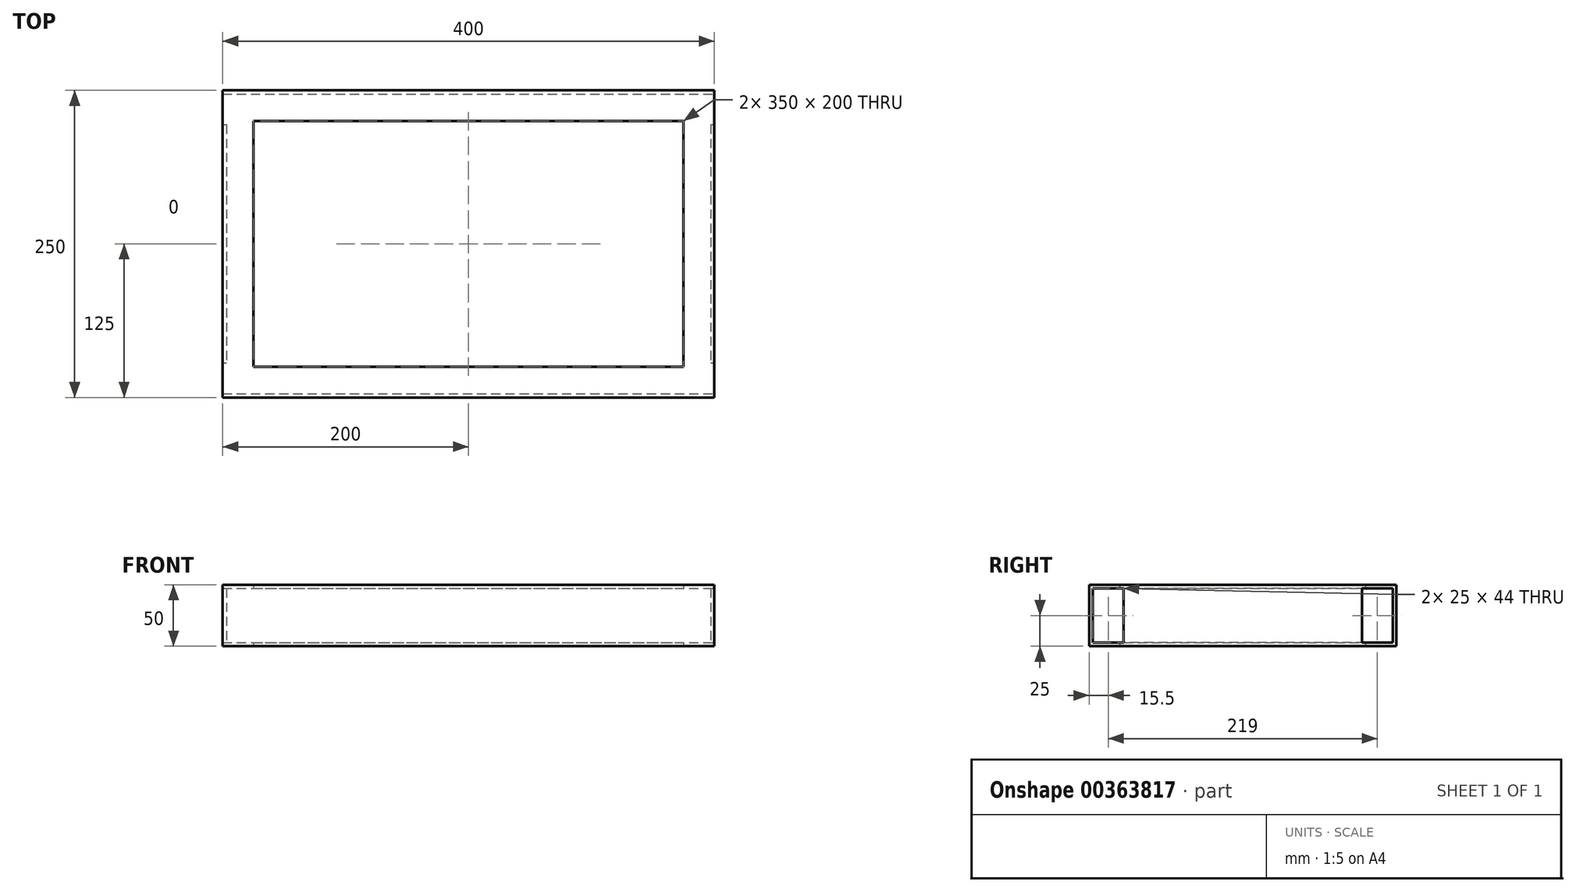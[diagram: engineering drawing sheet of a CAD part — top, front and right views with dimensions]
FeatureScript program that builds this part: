
annotation { "Feature Type Name" : "Feature", "Feature Type Description" : "" }
export const myFeature = defineFeature(function(context is Context, id is Id, definition is map)
    precondition{}
    {
        {
            var Q0;
            Q0=qCreatedBy(makeId("Top.planeOp"),FACE);
            var sketch = newSketch(context, id + "F0", { "sketchPlane" : qUnion([Q0])});
            skLineSegment(sketch, "E0.bottom", {"start": v(-200, 125) * mm, "end": v(200, 125) * mm});
            skLineSegment(sketch, "E0.top", {"start": v(-200, -125) * mm, "end": v(200, -125) * mm});
            skLineSegment(sketch, "E0.left", {"start": v(-200, 125) * mm, "end": v(-200, -125) * mm});
            skLineSegment(sketch, "E0.right", {"start": v(200, 125) * mm, "end": v(200, -125) * mm});
            skPoint(sketch, "E0.middle", {"position": v(0, 0) * mm});
            skLineSegment(sketch, "E1.bottom", {"start": v(-175, 100) * mm, "end": v(175, 100) * mm});
            skLineSegment(sketch, "E1.top", {"start": v(-175, -100) * mm, "end": v(175, -100) * mm});
            skLineSegment(sketch, "E1.left", {"start": v(-175, 100) * mm, "end": v(-175, -100) * mm});
            skLineSegment(sketch, "E1.right", {"start": v(175, 100) * mm, "end": v(175, -100) * mm});
            skLineSegment(sketch, "E2", {"start": v(-175, 33.87) * mm, "end": v(-200, 33.87) * mm, "construction": true});
            skLineSegment(sketch, "E3", {"start": v(-7.97, 100) * mm, "end": v(-7.97, 125) * mm, "construction": true});
            skLineSegment(sketch, "E4", {"start": v(-82.12, -100) * mm, "end": v(-82.12, -125) * mm, "construction": true});
            skLineSegment(sketch, "E5", {"start": v(175, -34.9) * mm, "end": v(200, -34.9) * mm, "construction": true});
            skSolve(sketch);
        }
        {
            var Q0;
            Q0=makeQuery(id+"F0.imprint","IMPRINT",FACE,{"disambiguationData":[TD([[makeQuery(id+"F0.imprint","IMPRINT",EDGE,{"derivedFrom":sQuery(id+"F0.wireOp",EDGE,"E0.bottom")}),-1.0]])]});
            extrude(context, id + "F1", {"entities" : qUnion([Q0]), "depth" : 50 * mm});
        }
        {
            var Q0;
            Q0=makeQuery(id+"F1.opExtrude","SWEPT_FACE",FACE,{"disambiguationData":[OSD([sQuery(id+"F0.wireOp",EDGE,"E0.top")])]});
            var sketch = newSketch(context, id + "F2", { "sketchPlane" : qUnion([Q0])});
            skLineSegment(sketch, "E6.bottom", {"start": v(197, 47) * mm, "end": v(172, 47) * mm});
            skLineSegment(sketch, "E6.top", {"start": v(197, 3) * mm, "end": v(172, 3) * mm});
            skLineSegment(sketch, "E6.left", {"start": v(197, 47) * mm, "end": v(197, 3) * mm});
            skLineSegment(sketch, "E6.right", {"start": v(172, 47) * mm, "end": v(172, 3) * mm});
            skLineSegment(sketch, "E7", {"start": v(197, 27.18) * mm, "end": v(200, 27.18) * mm, "construction": true});
            skLineSegment(sketch, "E8", {"start": v(108.69, 47) * mm, "end": v(108.69, 50) * mm, "construction": true});
            skLineSegment(sketch, "E9", {"start": v(106.18, 3) * mm, "end": v(106.18, 0) * mm, "construction": true});
            skLineSegment(sketch, "E10.MirrorCS", {"start": v(-172, 47) * mm, "end": v(-172, 3) * mm});
            skLineSegment(sketch, "E11.MirrorCS", {"start": v(-197, 47) * mm, "end": v(-172, 47) * mm});
            skLineSegment(sketch, "E12.MirrorCS", {"start": v(-197, 47) * mm, "end": v(-197, 3) * mm});
            skLineSegment(sketch, "E13.MirrorCS", {"start": v(-197, 3) * mm, "end": v(-172, 3) * mm});
            skSolve(sketch);
        }
        {
            var Q0;
            Q0 = qSketchRegion(id + "F2", true);
            var Q1;
            Q1=makeQuery(id+"F1.opExtrude","SWEPT_FACE",FACE,{"disambiguationData":[OSD([sQuery(id+"F0.wireOp",EDGE,"E0.bottom")])]});
            extrude(context, id + "F3", {"entities" : qUnion([Q0]), "operationType" : NewBodyOperationType.REMOVE, "endBound" : BoundingType.UP_TO_SURFACE, "oppositeDirection" : true, "endBoundEntityFace" : qUnion([Q1]), "depth" : 250 * mm});
        }
        {
            var Q0;
            Q0=makeQuery(id+"F1.opExtrude","SWEPT_FACE",FACE,{"disambiguationData":[OSD([sQuery(id+"F0.wireOp",EDGE,"E0.right")])]});
            var sketch = newSketch(context, id + "F4", { "sketchPlane" : qUnion([Q0])});
            skLineSegment(sketch, "E14.bottom", {"start": v(97, 3) * mm, "end": v(122, 3) * mm});
            skLineSegment(sketch, "E14.top", {"start": v(97, 47) * mm, "end": v(122, 47) * mm});
            skLineSegment(sketch, "E14.left", {"start": v(97, 3) * mm, "end": v(97, 47) * mm});
            skLineSegment(sketch, "E14.right", {"start": v(122, 3) * mm, "end": v(122, 47) * mm});
            skLineSegment(sketch, "E15", {"start": v(111.7, 47) * mm, "end": v(111.7, 50) * mm, "construction": true});
            skLineSegment(sketch, "E16", {"start": v(122, 25) * mm, "end": v(125, 25) * mm, "construction": true});
            skLineSegment(sketch, "E17", {"start": v(112.78, 3) * mm, "end": v(112.78, 0) * mm, "construction": true});
            skLineSegment(sketch, "E18.MirrorCS", {"start": v(-97, 3) * mm, "end": v(-97, 47) * mm});
            skLineSegment(sketch, "E19.MirrorCS", {"start": v(-97, 47) * mm, "end": v(-122, 47) * mm});
            skLineSegment(sketch, "E20.MirrorCS", {"start": v(-122, 3) * mm, "end": v(-122, 47) * mm});
            skLineSegment(sketch, "E21.MirrorCS", {"start": v(-97, 3) * mm, "end": v(-122, 3) * mm});
            skSolve(sketch);
        }
        {
            var Q0;
            Q0=makeQuery(id+"F4.imprint","IMPRINT",FACE,{"disambiguationData":[TD([[makeQuery(id+"F4.imprint","IMPRINT",EDGE,{"derivedFrom":sQuery(id+"F4.wireOp",EDGE,"E14.bottom")}),1.0]])]});
            var Q1;
            Q1=makeQuery(id+"F4.imprint","IMPRINT",FACE,{"disambiguationData":[TD([[makeQuery(id+"F4.imprint","IMPRINT",EDGE,{"derivedFrom":sQuery(id+"F4.wireOp",EDGE,"E18.MirrorCS")}),1.0]])]});
            var Q2;
            Q2=makeQuery(id+"F1.opExtrude","SWEPT_FACE",FACE,{"disambiguationData":[OSD([sQuery(id+"F0.wireOp",EDGE,"E0.left")])]});
            extrude(context, id + "F5", {"entities" : qUnion([Q0, Q1]), "operationType" : NewBodyOperationType.REMOVE, "endBound" : BoundingType.UP_TO_SURFACE, "oppositeDirection" : true, "endBoundEntityFace" : qUnion([Q2]), "depth" : 25 * mm});
        }
        {
            var Q0;
            Q0=makeQuery(id+"F3.boolean.opBoolean","COPY",FACE,{"disambiguationData":[TD([makeQuery(id+"F1.opExtrude","SWEPT_FACE",FACE,{"disambiguationData":[OSD([sQuery(id+"F0.wireOp",EDGE,"E0.top")])]})])],"derivedFrom":makeQuery(id+"F3.opExtrude","SWEPT_FACE",FACE,{"disambiguationData":[OSD([sQuery(id+"F2.wireOp",EDGE,"E6.right")])]})});
            extrude(context, id + "F6", {"entities" : qUnion([Q0]), "operationType" : NewBodyOperationType.ADD, "depth" : 25 * mm});
        }
        {
            var Q0;
            Q0=makeQuery(id+"F3.boolean.opBoolean","COPY",FACE,{"disambiguationData":[TD([makeQuery(id+"F1.opExtrude","SWEPT_FACE",FACE,{"disambiguationData":[OSD([sQuery(id+"F0.wireOp",EDGE,"E0.bottom")])]})])],"derivedFrom":makeQuery(id+"F3.opExtrude","SWEPT_FACE",FACE,{"disambiguationData":[OSD([sQuery(id+"F2.wireOp",EDGE,"E6.right")])]})});
            extrude(context, id + "F7", {"entities" : qUnion([Q0]), "operationType" : NewBodyOperationType.ADD, "depth" : 25 * mm});
        }
        {
            var Q0;
            Q0=makeQuery(id+"F3.boolean.opBoolean","COPY",FACE,{"disambiguationData":[TD([makeQuery(id+"F1.opExtrude","SWEPT_FACE",FACE,{"disambiguationData":[OSD([sQuery(id+"F0.wireOp",EDGE,"E0.bottom")])]})])],"derivedFrom":makeQuery(id+"F3.opExtrude","SWEPT_FACE",FACE,{"disambiguationData":[OSD([sQuery(id+"F2.wireOp",EDGE,"E10.MirrorCS")])]})});
            extrude(context, id + "F8", {"entities" : qUnion([Q0]), "operationType" : NewBodyOperationType.ADD, "depth" : 25 * mm});
        }
        {
            var Q0;
            Q0=makeQuery(id+"F3.boolean.opBoolean","COPY",FACE,{"disambiguationData":[TD([makeQuery(id+"F1.opExtrude","SWEPT_FACE",FACE,{"disambiguationData":[OSD([sQuery(id+"F0.wireOp",EDGE,"E0.top")])]})])],"derivedFrom":makeQuery(id+"F3.opExtrude","SWEPT_FACE",FACE,{"disambiguationData":[OSD([sQuery(id+"F2.wireOp",EDGE,"E10.MirrorCS")])]})});
            extrude(context, id + "F9", {"entities" : qUnion([Q0]), "operationType" : NewBodyOperationType.ADD, "depth" : 25 * mm});
        }
    });
